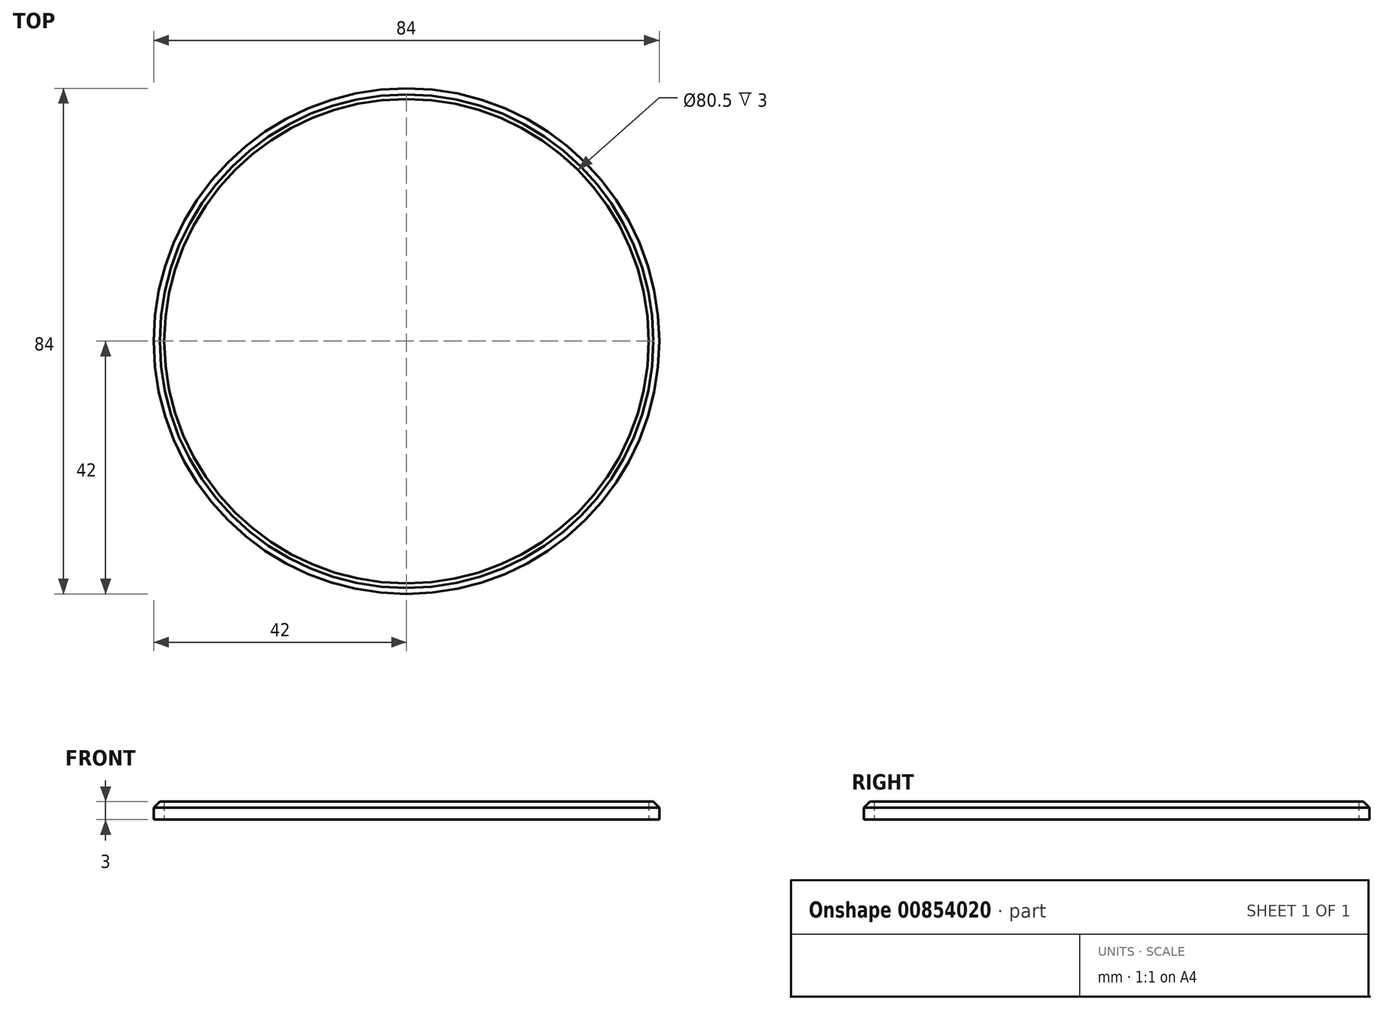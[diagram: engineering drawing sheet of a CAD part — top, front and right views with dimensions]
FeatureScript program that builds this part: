
annotation { "Feature Type Name" : "Feature", "Feature Type Description" : "" }
export const myFeature = defineFeature(function(context is Context, id is Id, definition is map)
    precondition{}
    {
        {
            var Q0;
            Q0=qCreatedBy(makeId("Top.planeOp"),FACE);
            var sketch = newSketch(context, id + "F0", { "sketchPlane" : qUnion([Q0])});
            skCircle(sketch, "E0", {"center": v(0, 0) * mm, "radius": 42 * mm});
            skSolve(sketch);
        }
        {
            var Q0;
            Q0=qCreatedBy(makeId("Top.planeOp"),FACE);
            var sketch = newSketch(context, id + "F1", { "sketchPlane" : qUnion([Q0])});
            skCircle(sketch, "E1", {"center": v(0, 0) * mm, "radius": 40.25 * mm});
            skSolve(sketch);
        }
        {
            var Q0;
            Q0=makeQuery(id+"F0.imprint","IMPRINT",FACE,{"disambiguationData":[TD([[makeQuery(id+"F0.imprint","IMPRINT",EDGE,{"derivedFrom":sQuery(id+"F0.wireOp",EDGE,"E0")}),1.0]])]});
            extrude(context, id + "F2", {"entities" : qUnion([Q0]), "depth" : 3 * mm, "offsetDistance" : 25 * mm});
        }
        {
            var Q0;
            Q0=makeQuery(id+"F1.imprint","IMPRINT",FACE,{"disambiguationData":[TD([[makeQuery(id+"F1.imprint","IMPRINT",EDGE,{"derivedFrom":sQuery(id+"F1.wireOp",EDGE,"E1")}),1.0]])]});
            extrude(context, id + "F3", {"entities" : qUnion([Q0]), "operationType" : NewBodyOperationType.REMOVE, "depth" : 16 * mm, "offsetDistance" : 25 * mm});
        }
        {
            var Q0;
            Q0=makeQuery(id+"F3.boolean.opBoolean","COPY",EDGE,{"derivedFrom":makeQuery(id+"F3.opExtrude","CAP_EDGE",EDGE,{"disambiguationData":[OSD([sQuery(id+"F1.wireOp",EDGE,"E1")])],"isStart":true})});
            var Q1;
            Q1=makeQuery(id+"F2.opExtrude","CAP_EDGE",EDGE,{"disambiguationData":[OSD([sQuery(id+"F0.wireOp",EDGE,"E0")])],"isStart":false});
            chamfer(context, id + "F4", {"entities" : qUnion([Q0, Q1]), "width" : 1 * mm, "tangentPropagation" : true});
        }
        {
            var Q0;
            Q0=qCreatedBy(makeId("Front.planeOp"),FACE);
            var sketch = newSketch(context, id + "F5", { "sketchPlane" : qUnion([Q0])});
            skLineSegment(sketch, "E2.bottom", {"start": v(0, 15) * mm, "end": v(-7, 15) * mm});
            skLineSegment(sketch, "E2.top", {"start": v(0, 12) * mm, "end": v(-7, 12) * mm});
            skLineSegment(sketch, "E2.left", {"start": v(0, 15) * mm, "end": v(0, 12) * mm});
            skLineSegment(sketch, "E2.right", {"start": v(-7, 15) * mm, "end": v(-7, 12) * mm});
            skSolve(sketch);
        }
        {
            var Q0;
            Q0=qSketchRegion(id+"F5",true);
            extrude(context, id + "F6", {"entities" : qUnion([Q0]), "operationType" : NewBodyOperationType.REMOVE, "oppositeDirection" : true, "depth" : 50 * mm, "offsetDistance" : 25 * mm});
        }
    });
